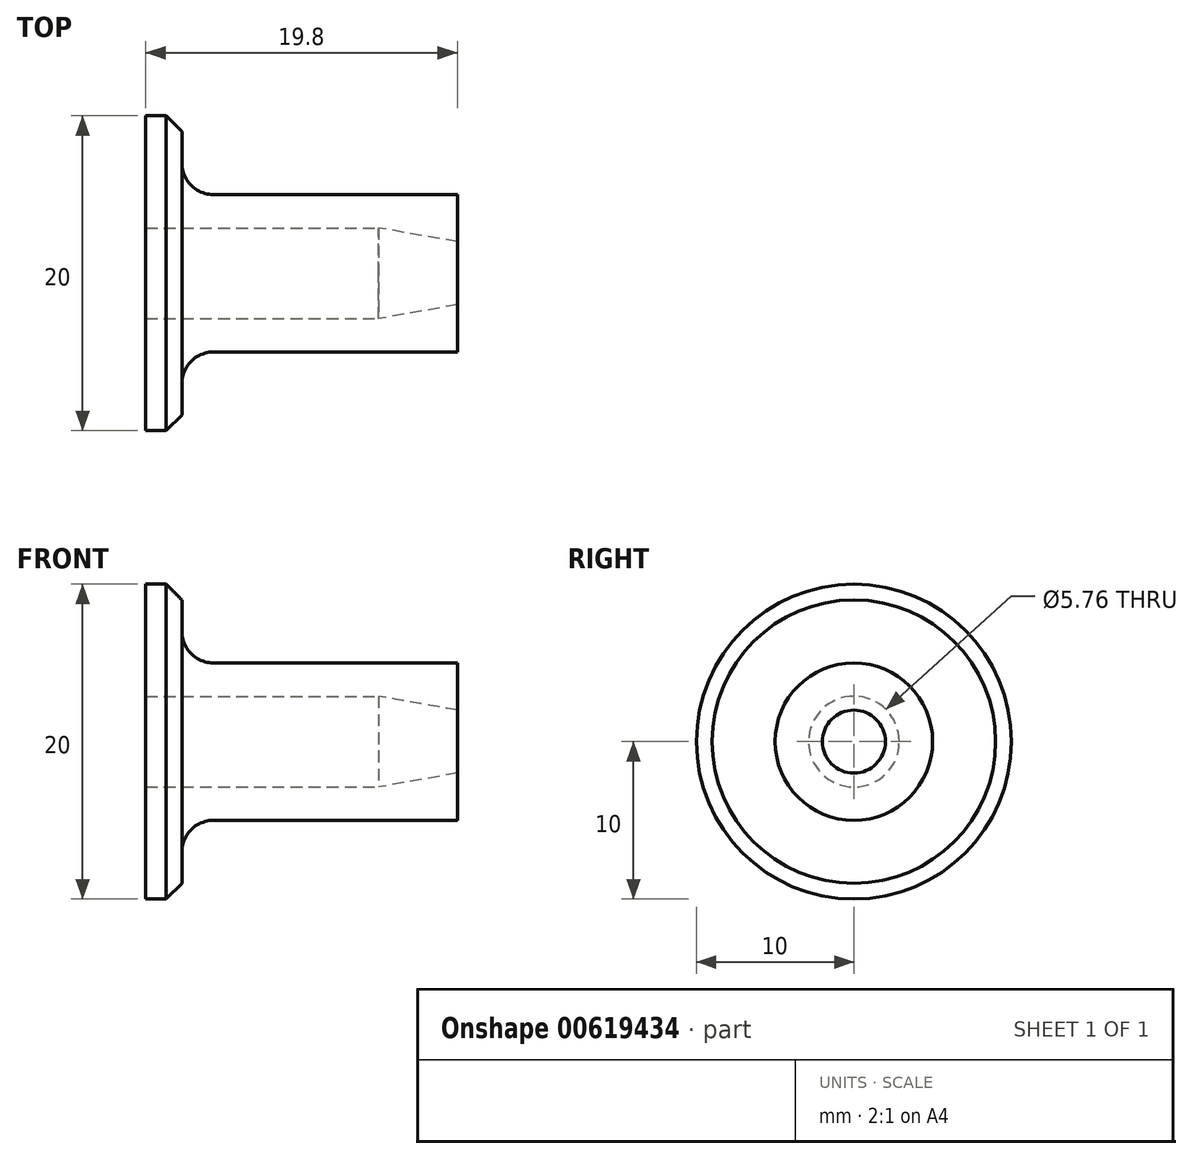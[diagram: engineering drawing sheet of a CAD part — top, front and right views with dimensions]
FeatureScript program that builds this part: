
annotation { "Feature Type Name" : "Feature", "Feature Type Description" : "" }
export const myFeature = defineFeature(function(context is Context, id is Id, definition is map)
    precondition{}
    {
        {
            var Q0;
            Q0=qCreatedBy(makeId("Front.planeOp"),FACE);
            var sketch = newSketch(context, id + "F0", { "sketchPlane" : qUnion([Q0])});
            skLineSegment(sketch, "E0.bottom", {"start": v(0, 0) * mm, "end": v(2.3, 0) * mm});
            skLineSegment(sketch, "E0.top", {"start": v(0, 10) * mm, "end": v(2.3, 10) * mm});
            skLineSegment(sketch, "E0.left", {"start": v(0, 0) * mm, "end": v(0, 10) * mm});
            skLineSegment(sketch, "E0.right", {"start": v(2.3, 0) * mm, "end": v(2.3, 10) * mm});
            skLineSegment(sketch, "E1.bottom", {"start": v(2.3, 0) * mm, "end": v(19.8, 0) * mm});
            skLineSegment(sketch, "E1.top", {"start": v(2.3, 5) * mm, "end": v(19.8, 5) * mm});
            skLineSegment(sketch, "E1.left", {"start": v(2.3, 0) * mm, "end": v(2.3, 5) * mm});
            skLineSegment(sketch, "E1.right", {"start": v(19.8, 0) * mm, "end": v(19.8, 5) * mm});
            skLineSegment(sketch, "E2", {"start": v(14.8, 2.88) * mm, "end": v(14.8, 0) * mm});
            skLineSegment(sketch, "E3", {"start": v(14.8, 2.88) * mm, "end": v(19.8, 2) * mm});
            skSolve(sketch);
        }
        {
            var Q0;
            Q0=makeQuery(id+"F0.imprint","IMPRINT",FACE,{"disambiguationData":[TD([[makeQuery(id+"F0.imprint","IMPRINT",EDGE,{"derivedFrom":sQuery(id+"F0.wireOp",EDGE,"E0.bottom")}),1.0]])]});
            var Q1;
            {var subQ1=sQuery(id+"F0.wireOp",EDGE,"E1.top");Q1=makeQuery(id+"F0.imprint","IMPRINT",FACE,{"disambiguationData":[TD([[makeQuery(id+"F0.imprint","IMPRINT",EDGE,{"derivedFrom":subQ1}),-1.0]])]});}
            var Q2;
            Q2=sQuery(id+"F0.wireOp",EDGE,"E1.bottom");
            revolve(context, id + "F1", {"entities" : qUnion([Q0, Q1]), "axis" : qUnion([Q2]), "revolveType" : RevolveType.FULL});
        }
        {
            var Q0;
            Q0=makeQuery(id+"F1.opRevolve","SWEPT_EDGE",EDGE,{"disambiguationData":[OSD([sQuery(id+"F0.wireOp",EDGE,"E0.right"),sQuery(id+"F0.wireOp",EDGE,"E1.top"),sQuery(id+"F0.wireOp",EDGE,"E1.left")])]});
            fillet(context, id + "F2", {"entities" : qUnion([Q0]), "radius" : 2 * mm, "tangentPropagation" : true, "allowEdgeOverflow" : false});
        }
        {
            var Q0;
            Q0=makeQuery(id+"F1.opRevolve","SWEPT_EDGE",EDGE,{"disambiguationData":[OSD([sQuery(id+"F0.wireOp",EDGE,"E0.top"),sQuery(id+"F0.wireOp",EDGE,"E0.right")])]});
            chamfer(context, id + "F3", {"entities" : qUnion([Q0]), "width" : 1 * mm, "tangentPropagation" : true});
        }
        {
            var Q0;
            Q0=makeQuery(id+"F1.opRevolve","SWEPT_FACE",FACE,{"disambiguationData":[OSD([sQuery(id+"F0.wireOp",EDGE,"E2")])]});
            extrude(context, id + "F4", {"entities" : qUnion([Q0]), "operationType" : NewBodyOperationType.REMOVE, "oppositeDirection" : true, "depth" : 25 * mm, "offsetDistance" : 25 * mm});
        }
    });
